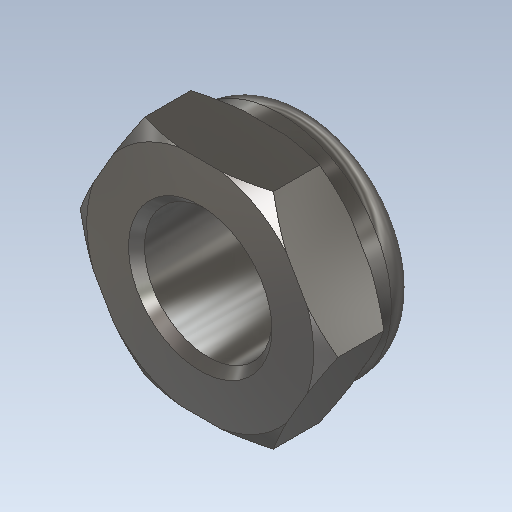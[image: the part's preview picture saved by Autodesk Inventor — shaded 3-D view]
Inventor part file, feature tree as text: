
AUTODESK INVENTOR PART (.ipt)
format: ipt  version: 2020.1 (Build 241239000, 239)  size: 232,960 bytes
history: native  units: mm
features: sketch x4, extrude x3, fillet x2, other x1, revolve x1, chamfer x1
ambient origin geometry x8: Origin, YZ Plane, XZ Plane, XY Plane, X Axis, Y Axis, Z Axis, Center Point
bodies: Body1 (feature_tree)
feature tree (12):
  other  "Твердое тело1"
  extrude  "Выдавливание1"  Depth=8.0mm
  revolve  "Вращение1"
  extrude  "Выдавливание2"  Depth=14.0mm
  fillet  "Сопряжение1"  Radius=4.0mm
  extrude  "Выдавливание3"  TaperAngle=60.0deg  [1 undecoded]
  fillet  "Сопряжение2"  Radius=1.0mm
  chamfer  "Фаска2"  Distance=3.5mm
  sketch  "Эскиз1"
  sketch  "Эскиз2"
  sketch  "Эскиз3"
  sketch  "Эскиз4"
note: 1 required parameter value undecoded (feature->parameter linkage not recoverable at this tier; creation-order binding heuristic only, values carry confidence <= 0.55)
